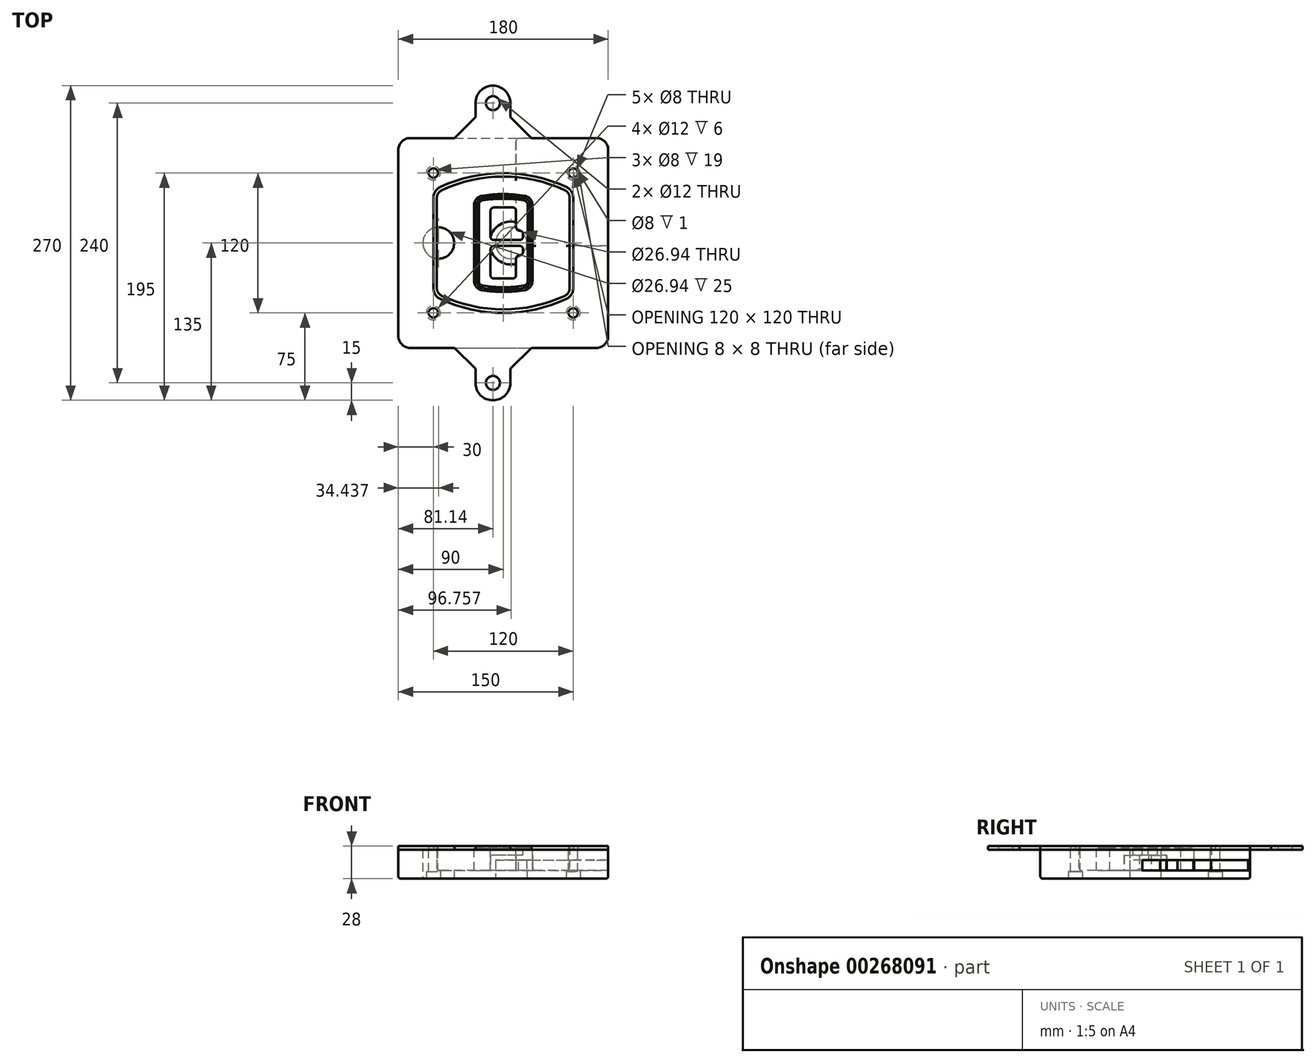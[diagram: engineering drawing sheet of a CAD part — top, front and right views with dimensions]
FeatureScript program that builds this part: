
annotation { "Feature Type Name" : "Feature", "Feature Type Description" : "" }
export const myFeature = defineFeature(function(context is Context, id is Id, definition is map)
    precondition{}
    {
        {
            var Q0;
            Q0=qCreatedBy(makeId("Top.planeOp"),FACE);
            var sketch = newSketch(context, id + "F0", { "sketchPlane" : qUnion([Q0])});
            skPoint(sketch, "E0.rect.middle", {"position": v(0, 0) * mm});
            skLineSegment(sketch, "E1.bottom", {"start": v(-80, -90) * mm, "end": v(80, -90) * mm});
            skLineSegment(sketch, "E1.top", {"start": v(-80, 90) * mm, "end": v(80, 90) * mm});
            skLineSegment(sketch, "E1.left", {"start": v(-90, -80) * mm, "end": v(-90, 80) * mm});
            skLineSegment(sketch, "E1.right", {"start": v(90, -80) * mm, "end": v(90, 80) * mm});
            skLineSegment(sketch, "E2", {"start": v(-90, 90) * mm, "end": v(90, -90) * mm, "construction": true});
            skLineSegment(sketch, "E3", {"start": v(90, 90) * mm, "end": v(-90, -90) * mm, "construction": true});
            skCircle(sketch, "E4", {"center": v(-60, 60) * mm, "radius": 4 * mm});
            skCircle(sketch, "E5", {"center": v(60, 60) * mm, "radius": 4 * mm});
            skCircle(sketch, "E6", {"center": v(60, -60) * mm, "radius": 4 * mm});
            skCircle(sketch, "E7", {"center": v(-60, -60) * mm, "radius": 4 * mm});
            skLineSegment(sketch, "E8", {"start": v(-60, 60) * mm, "end": v(60, 60) * mm, "construction": true});
            skLineSegment(sketch, "E9", {"start": v(60, 60) * mm, "end": v(60, -60) * mm, "construction": true});
            skLineSegment(sketch, "E10", {"start": v(60, -60) * mm, "end": v(-60, -60) * mm, "construction": true});
            skLineSegment(sketch, "E11", {"start": v(-60, -60) * mm, "end": v(-60, 60) * mm, "construction": true});
            skLineSegment(sketch, "E12", {"start": v(-60, 38.83) * mm, "end": v(-60, -38.83) * mm});
            skLineSegment(sketch, "E13", {"start": v(60, 38.83) * mm, "end": v(60, -38.83) * mm});
            skArc(sketch, "E14", {"start": v(54.26, 47.88) * mm, "mid": v(0, 60) * mm, "end": v(-54.26, 47.88) * mm});
            skArc(sketch, "E15", {"start": v(-54.26, -47.88) * mm, "mid": v(0, -60) * mm, "end": v(54.26, -47.88) * mm});
            skLineSegment(sketch, "E16", {"start": v(-60, 0) * mm, "end": v(60, 0) * mm, "construction": true});
            skPoint(sketch, "E17.visualSharp", {"position": v(-60, -45) * mm});
            skArc(sketch, "E17.filletArc", {"start": v(-60, -38.83) * mm, "mid": v(-58.44, -44.2) * mm, "end": v(-54.26, -47.88) * mm});
            skPoint(sketch, "E18.visualSharp", {"position": v(-60, 45) * mm});
            skArc(sketch, "E18.filletArc", {"start": v(-54.26, 47.88) * mm, "mid": v(-58.44, 44.2) * mm, "end": v(-60, 38.83) * mm});
            skPoint(sketch, "E19.visualSharp", {"position": v(60, 45) * mm});
            skArc(sketch, "E19.filletArc", {"start": v(60, 38.83) * mm, "mid": v(58.44, 44.2) * mm, "end": v(54.26, 47.88) * mm});
            skPoint(sketch, "E20.visualSharp", {"position": v(60, -45) * mm});
            skArc(sketch, "E20.filletArc", {"start": v(54.26, -47.88) * mm, "mid": v(58.44, -44.2) * mm, "end": v(60, -38.83) * mm});
            skPoint(sketch, "E21.visualSharp", {"position": v(-90, 90) * mm});
            skArc(sketch, "E21.filletArc", {"start": v(-80, 90) * mm, "mid": v(-87.07, 87.07) * mm, "end": v(-90, 80) * mm});
            skPoint(sketch, "E22.visualSharp", {"position": v(90, 90) * mm});
            skArc(sketch, "E22.filletArc", {"start": v(90, 80) * mm, "mid": v(87.07, 87.07) * mm, "end": v(80, 90) * mm});
            skPoint(sketch, "E23.visualSharp", {"position": v(90, -90) * mm});
            skArc(sketch, "E23.filletArc", {"start": v(80, -90) * mm, "mid": v(87.07, -87.07) * mm, "end": v(90, -80) * mm});
            skPoint(sketch, "E24.visualSharp", {"position": v(-90, -90) * mm});
            skArc(sketch, "E24.filletArc", {"start": v(-90, -80) * mm, "mid": v(-87.07, -87.07) * mm, "end": v(-80, -90) * mm});
            skArc(sketch, "E25.0", {"start": v(57, 38.83) * mm, "mid": v(55.9, 42.58) * mm, "end": v(52.98, 45.17) * mm});
            skLineSegment(sketch, "E25.1", {"start": v(57, 38.83) * mm, "end": v(57, -38.83) * mm});
            skArc(sketch, "E25.2", {"start": v(52.98, -45.17) * mm, "mid": v(55.9, -42.58) * mm, "end": v(57, -38.83) * mm});
            skArc(sketch, "E25.3", {"start": v(-52.98, -45.17) * mm, "mid": v(0, -57) * mm, "end": v(52.98, -45.17) * mm});
            skArc(sketch, "E25.4", {"start": v(-57, -38.83) * mm, "mid": v(-55.9, -42.58) * mm, "end": v(-52.98, -45.17) * mm});
            skArc(sketch, "E25.5", {"start": v(52.98, 45.17) * mm, "mid": v(0, 57) * mm, "end": v(-52.98, 45.17) * mm});
            skLineSegment(sketch, "E25.6", {"start": v(-57, 38.83) * mm, "end": v(-57, -38.83) * mm});
            skArc(sketch, "E25.7", {"start": v(-52.98, 45.17) * mm, "mid": v(-55.9, 42.58) * mm, "end": v(-57, 38.83) * mm});
            skArc(sketch, "E26.0", {"start": v(-55.96, 51.5) * mm, "mid": v(-61.82, 46.33) * mm, "end": v(-64, 38.83) * mm});
            skArc(sketch, "E26.1", {"start": v(55.96, 51.5) * mm, "mid": v(0, 64) * mm, "end": v(-55.96, 51.5) * mm});
            skArc(sketch, "E26.2", {"start": v(64, 38.83) * mm, "mid": v(61.82, 46.33) * mm, "end": v(55.96, 51.5) * mm});
            skLineSegment(sketch, "E26.3", {"start": v(64, 38.83) * mm, "end": v(64, -38.83) * mm});
            skArc(sketch, "E26.4", {"start": v(55.96, -51.5) * mm, "mid": v(61.82, -46.33) * mm, "end": v(64, -38.83) * mm});
            skLineSegment(sketch, "E26.5", {"start": v(-64, 38.83) * mm, "end": v(-64, -38.83) * mm});
            skArc(sketch, "E26.6", {"start": v(-55.96, -51.5) * mm, "mid": v(0, -64) * mm, "end": v(55.96, -51.5) * mm});
            skArc(sketch, "E26.7", {"start": v(-64, -38.83) * mm, "mid": v(-61.82, -46.33) * mm, "end": v(-55.96, -51.5) * mm});
            skSolve(sketch);
        }
        {
            var Q0;
            Q0=makeQuery(id+"F0.imprint","IMPRINT",FACE,{"disambiguationData":[TD([[makeQuery(id+"F0.imprint","IMPRINT",EDGE,{"derivedFrom":sQuery(id+"F0.wireOp",EDGE,"E1.bottom")}),1.0]])]});
            var Q1;
            Q1=makeQuery(id+"F0.imprint","IMPRINT",FACE,{"disambiguationData":[TD([[makeQuery(id+"F0.imprint","IMPRINT",EDGE,{"derivedFrom":sQuery(id+"F0.wireOp",EDGE,"E12")}),1.0]])]});
            var Q2;
            Q2=makeQuery(id+"F0.imprint","IMPRINT",FACE,{"disambiguationData":[TD([[makeQuery(id+"F0.imprint","IMPRINT",EDGE,{"derivedFrom":sQuery(id+"F0.wireOp",EDGE,"E25.0")}),1.0]])]});
            var Q3;
            Q3=makeQuery(id+"F0.imprint","IMPRINT",FACE,{"disambiguationData":[TD([[makeQuery(id+"F0.imprint","IMPRINT",EDGE,{"derivedFrom":sQuery(id+"F0.wireOp",EDGE,"E12")}),-1.0]])]});
            extrude(context, id + "F1", {"entities" : qUnion([Q0, Q1, Q2, Q3]), "oppositeDirection" : true, "depth" : 25 * mm});
        }
        {
            var Q0;
            Q0=makeQuery(id+"F0.imprint","IMPRINT",FACE,{"disambiguationData":[TD([[makeQuery(id+"F0.imprint","IMPRINT",EDGE,{"derivedFrom":sQuery(id+"F0.wireOp",EDGE,"E12")}),1.0]])]});
            extrude(context, id + "F2", {"entities" : qUnion([Q0]), "operationType" : NewBodyOperationType.ADD, "depth" : 3 * mm});
        }
        {
            var Q0;
            Q0=makeQuery(id+"F0.imprint","IMPRINT",FACE,{"disambiguationData":[TD([[makeQuery(id+"F0.imprint","IMPRINT",EDGE,{"derivedFrom":sQuery(id+"F0.wireOp",EDGE,"E25.0")}),1.0]])]});
            extrude(context, id + "F3", {"entities" : qUnion([Q0]), "operationType" : NewBodyOperationType.REMOVE, "oppositeDirection" : true, "depth" : 18 * mm});
        }
        {
            var Q0;
            Q0=makeQuery(id+"F2.opExtrude","CAP_FACE",FACE,{"disambiguationData":[OSD([sQuery(id+"F0.wireOp",EDGE,"E12"),sQuery(id+"F0.wireOp",EDGE,"E13"),sQuery(id+"F0.wireOp",EDGE,"E14"),sQuery(id+"F0.wireOp",EDGE,"E15"),sQuery(id+"F0.wireOp",EDGE,"E17.filletArc"),sQuery(id+"F0.wireOp",EDGE,"E18.filletArc"),sQuery(id+"F0.wireOp",EDGE,"E19.filletArc"),sQuery(id+"F0.wireOp",EDGE,"E20.filletArc"),sQuery(id+"F0.wireOp",EDGE,"E25.0"),sQuery(id+"F0.wireOp",EDGE,"E25.1"),sQuery(id+"F0.wireOp",EDGE,"E25.2"),sQuery(id+"F0.wireOp",EDGE,"E25.3"),sQuery(id+"F0.wireOp",EDGE,"E25.4"),sQuery(id+"F0.wireOp",EDGE,"E25.5"),sQuery(id+"F0.wireOp",EDGE,"E25.6"),sQuery(id+"F0.wireOp",EDGE,"E25.7")])],"isStart":false});
            var sketch = newSketch(context, id + "F4", { "sketchPlane" : qUnion([Q0])});
            skArc(sketch, "E27.0", {"start": v(-18.34, -40.45) * mm, "mid": v(0, -42) * mm, "end": v(18.34, -40.45) * mm});
            skArc(sketch, "E28.0", {"start": v(18.34, 40.45) * mm, "mid": v(0, 42) * mm, "end": v(-18.34, 40.45) * mm});
            skLineSegment(sketch, "E29", {"start": v(-25, 32.57) * mm, "end": v(-25, -32.57) * mm});
            skLineSegment(sketch, "E30", {"start": v(25, 32.57) * mm, "end": v(25, -32.57) * mm});
            skLineSegment(sketch, "E31", {"start": v(-25, 39.1) * mm, "end": v(25, 39.1) * mm, "construction": true});
            skLineSegment(sketch, "E32", {"start": v(-25, -39.1) * mm, "end": v(25, -39.1) * mm, "construction": true});
            skPoint(sketch, "E33.visualSharp", {"position": v(-25, 39.1) * mm});
            skArc(sketch, "E33.filletArc", {"start": v(-18.34, 40.45) * mm, "mid": v(-23.11, 37.73) * mm, "end": v(-25, 32.57) * mm});
            skPoint(sketch, "E34.visualSharp", {"position": v(25, 39.1) * mm});
            skArc(sketch, "E34.filletArc", {"start": v(25, 32.57) * mm, "mid": v(23.11, 37.73) * mm, "end": v(18.34, 40.45) * mm});
            skPoint(sketch, "E35.visualSharp", {"position": v(25, -39.1) * mm});
            skArc(sketch, "E35.filletArc", {"start": v(18.34, -40.45) * mm, "mid": v(23.11, -37.73) * mm, "end": v(25, -32.57) * mm});
            skPoint(sketch, "E36.visualSharp", {"position": v(-25, -39.1) * mm});
            skArc(sketch, "E36.filletArc", {"start": v(-25, -32.57) * mm, "mid": v(-23.11, -37.73) * mm, "end": v(-18.34, -40.45) * mm});
            skArc(sketch, "E37.0", {"start": v(52.98, 45.17) * mm, "mid": v(0, 57) * mm, "end": v(-52.98, 45.17) * mm});
            skArc(sketch, "E37.1", {"start": v(-52.98, 45.17) * mm, "mid": v(-55.9, 42.58) * mm, "end": v(-57, 38.83) * mm});
            skLineSegment(sketch, "E37.2", {"start": v(-57, 38.83) * mm, "end": v(-57, -38.83) * mm});
            skArc(sketch, "E37.3", {"start": v(-57, -38.83) * mm, "mid": v(-55.9, -42.58) * mm, "end": v(-52.98, -45.17) * mm});
            skArc(sketch, "E37.4", {"start": v(-52.98, -45.17) * mm, "mid": v(0, -57) * mm, "end": v(52.98, -45.17) * mm});
            skArc(sketch, "E37.5", {"start": v(52.98, -45.17) * mm, "mid": v(55.9, -42.58) * mm, "end": v(57, -38.83) * mm});
            skLineSegment(sketch, "E37.6", {"start": v(57, 38.83) * mm, "end": v(57, -38.83) * mm});
            skArc(sketch, "E37.7", {"start": v(57, 38.83) * mm, "mid": v(55.9, 42.58) * mm, "end": v(52.98, 45.17) * mm});
            skLineSegment(sketch, "E38.0", {"start": v(23, 32.57) * mm, "end": v(23, -32.57) * mm});
            skArc(sketch, "E38.1", {"start": v(18, -38.48) * mm, "mid": v(21.58, -36.44) * mm, "end": v(23, -32.57) * mm});
            skArc(sketch, "E38.2", {"start": v(-18, -38.48) * mm, "mid": v(0, -40) * mm, "end": v(18, -38.48) * mm});
            skArc(sketch, "E38.3", {"start": v(-23, -32.57) * mm, "mid": v(-21.58, -36.44) * mm, "end": v(-18, -38.48) * mm});
            skLineSegment(sketch, "E38.4", {"start": v(-23, 32.57) * mm, "end": v(-23, -32.57) * mm});
            skArc(sketch, "E38.5", {"start": v(23, 32.57) * mm, "mid": v(21.58, 36.44) * mm, "end": v(18, 38.48) * mm});
            skArc(sketch, "E38.6", {"start": v(-18, 38.48) * mm, "mid": v(-21.58, 36.44) * mm, "end": v(-23, 32.57) * mm});
            skArc(sketch, "E38.7", {"start": v(18, 38.48) * mm, "mid": v(0, 40) * mm, "end": v(-18, 38.48) * mm});
            skArc(sketch, "E39.0", {"start": v(21, 32.57) * mm, "mid": v(20.06, 35.15) * mm, "end": v(17.67, 36.5) * mm});
            skLineSegment(sketch, "E39.1", {"start": v(21, 32.57) * mm, "end": v(21, -32.57) * mm});
            skArc(sketch, "E39.2", {"start": v(17.67, -36.5) * mm, "mid": v(20.06, -35.15) * mm, "end": v(21, -32.57) * mm});
            skArc(sketch, "E39.3", {"start": v(-17.67, -36.5) * mm, "mid": v(0, -38) * mm, "end": v(17.67, -36.5) * mm});
            skArc(sketch, "E39.4", {"start": v(-21, -32.57) * mm, "mid": v(-20.06, -35.15) * mm, "end": v(-17.67, -36.5) * mm});
            skArc(sketch, "E39.5", {"start": v(17.67, 36.5) * mm, "mid": v(0, 38) * mm, "end": v(-17.67, 36.5) * mm});
            skLineSegment(sketch, "E39.6", {"start": v(-21, 32.57) * mm, "end": v(-21, -32.57) * mm});
            skArc(sketch, "E39.7", {"start": v(-17.67, 36.5) * mm, "mid": v(-20.06, 35.15) * mm, "end": v(-21, 32.57) * mm});
            skLineSegment(sketch, "E40", {"start": v(-25, 0) * mm, "end": v(25, 0) * mm, "construction": true});
            skLineSegment(sketch, "E41", {"start": v(-11, 5.5) * mm, "end": v(-11, 27.5) * mm});
            skLineSegment(sketch, "E42", {"start": v(-8, 30.5) * mm, "end": v(8, 30.5) * mm});
            skLineSegment(sketch, "E43", {"start": v(11, 27.5) * mm, "end": v(11, 13.5) * mm});
            skLineSegment(sketch, "E44", {"start": v(14, 10.5) * mm, "end": v(14, 10.5) * mm});
            skLineSegment(sketch, "E45", {"start": v(17, 7.5) * mm, "end": v(17, 5.5) * mm});
            skLineSegment(sketch, "E46", {"start": v(14, 2.5) * mm, "end": v(-8, 2.5) * mm});
            skPoint(sketch, "E47.visualSharp", {"position": v(-11, 30.5) * mm});
            skArc(sketch, "E47.filletArc", {"start": v(-8, 30.5) * mm, "mid": v(-10.12, 29.62) * mm, "end": v(-11, 27.5) * mm});
            skPoint(sketch, "E48.visualSharp", {"position": v(11, 30.5) * mm});
            skArc(sketch, "E48.filletArc", {"start": v(11, 27.5) * mm, "mid": v(10.12, 29.62) * mm, "end": v(8, 30.5) * mm});
            skPoint(sketch, "E49.visualSharp", {"position": v(11, 10.5) * mm});
            skArc(sketch, "E49.filletArc", {"start": v(11, 13.5) * mm, "mid": v(11.88, 11.38) * mm, "end": v(14, 10.5) * mm});
            skPoint(sketch, "E50.visualSharp", {"position": v(17, 10.5) * mm});
            skArc(sketch, "E50.filletArc", {"start": v(17, 7.5) * mm, "mid": v(16.12, 9.62) * mm, "end": v(14, 10.5) * mm});
            skPoint(sketch, "E51.visualSharp", {"position": v(17, 2.5) * mm});
            skArc(sketch, "E51.filletArc", {"start": v(14, 2.5) * mm, "mid": v(16.12, 3.38) * mm, "end": v(17, 5.5) * mm});
            skPoint(sketch, "E52.visualSharp", {"position": v(-11, 2.5) * mm});
            skArc(sketch, "E52.filletArc", {"start": v(-11, 5.5) * mm, "mid": v(-10.12, 3.38) * mm, "end": v(-8, 2.5) * mm});
            skLineSegment(sketch, "E53.0.MirrorCS", {"start": v(14, -2.5) * mm, "end": v(-8, -2.5) * mm});
            skArc(sketch, "E54.0.MirrorCS", {"start": v(-11, -5.5) * mm, "mid": v(-10.12, -3.38) * mm, "end": v(-8, -2.5) * mm});
            skLineSegment(sketch, "E55.0.MirrorCS", {"start": v(-11, -5.5) * mm, "end": v(-11, -27.5) * mm});
            skArc(sketch, "E56.0.MirrorCS", {"start": v(-8, -30.5) * mm, "mid": v(-10.12, -29.62) * mm, "end": v(-11, -27.5) * mm});
            skLineSegment(sketch, "E57.0.MirrorCS", {"start": v(-8, -30.5) * mm, "end": v(8, -30.5) * mm});
            skArc(sketch, "E58.0.MirrorCS", {"start": v(11, -27.5) * mm, "mid": v(10.12, -29.62) * mm, "end": v(8, -30.5) * mm});
            skLineSegment(sketch, "E59.0.MirrorCS", {"start": v(11, -27.5) * mm, "end": v(11, -13.5) * mm});
            skArc(sketch, "E60.0.MirrorCS", {"start": v(11, -13.5) * mm, "mid": v(11.88, -11.38) * mm, "end": v(14, -10.5) * mm});
            skArc(sketch, "E61.0.MirrorCS", {"start": v(17, -7.5) * mm, "mid": v(16.12, -9.62) * mm, "end": v(14, -10.5) * mm});
            skLineSegment(sketch, "E62.0.MirrorCS", {"start": v(17, -7.5) * mm, "end": v(17, -5.5) * mm});
            skArc(sketch, "E63.0.MirrorCS", {"start": v(14, -2.5) * mm, "mid": v(16.12, -3.38) * mm, "end": v(17, -5.5) * mm});
            skSolve(sketch);
        }
        {
            var Q0;
            Q0=makeQuery(id+"F4.imprint","IMPRINT",FACE,{"disambiguationData":[TD([[makeQuery(id+"F4.imprint","IMPRINT",EDGE,{"derivedFrom":sQuery(id+"F4.wireOp",EDGE,"E27.0")}),1.0]])]});
            var Q1;
            Q1=makeQuery(id+"F4.imprint","IMPRINT",FACE,{"disambiguationData":[TD([[makeQuery(id+"F4.imprint","IMPRINT",EDGE,{"derivedFrom":sQuery(id+"F4.wireOp",EDGE,"E38.0")}),-1.0]])]});
            var Q2;
            Q2=makeQuery(id+"F4.imprint","IMPRINT",FACE,{"disambiguationData":[TD([[makeQuery(id+"F4.imprint","IMPRINT",EDGE,{"derivedFrom":sQuery(id+"F4.wireOp",EDGE,"E39.0")}),1.0]])]});
            extrude(context, id + "F5", {"entities" : qUnion([Q0, Q1, Q2]), "operationType" : NewBodyOperationType.ADD, "endBound" : BoundingType.UP_TO_NEXT, "oppositeDirection" : true, "depth" : 25 * mm});
        }
        {
            var Q0;
            Q0=makeQuery(id+"F4.imprint","IMPRINT",FACE,{"disambiguationData":[TD([[makeQuery(id+"F4.imprint","IMPRINT",EDGE,{"derivedFrom":sQuery(id+"F4.wireOp",EDGE,"E38.0")}),-1.0]])]});
            extrude(context, id + "F6", {"entities" : qUnion([Q0]), "operationType" : NewBodyOperationType.REMOVE, "oppositeDirection" : true, "depth" : 2 * mm});
        }
        {
            var Q0;
            Q0=makeQuery(id+"F1.opExtrude","CAP_FACE",FACE,{"disambiguationData":[OSD([sQuery(id+"F0.wireOp",EDGE,"E1.bottom"),sQuery(id+"F0.wireOp",EDGE,"E1.top"),sQuery(id+"F0.wireOp",EDGE,"E1.left"),sQuery(id+"F0.wireOp",EDGE,"E1.right"),sQuery(id+"F0.wireOp",EDGE,"E4"),sQuery(id+"F0.wireOp",EDGE,"E5"),sQuery(id+"F0.wireOp",EDGE,"E6"),sQuery(id+"F0.wireOp",EDGE,"E7"),sQuery(id+"F0.wireOp",EDGE,"E21.filletArc"),sQuery(id+"F0.wireOp",EDGE,"E22.filletArc"),sQuery(id+"F0.wireOp",EDGE,"E23.filletArc"),sQuery(id+"F0.wireOp",EDGE,"E24.filletArc")])],"isStart":false});
            var sketch = newSketch(context, id + "F7", { "sketchPlane" : qUnion([Q0])});
            skCircle(sketch, "E64", {"center": v(6.76, 0) * mm, "radius": 13.47 * mm});
            skCircle(sketch, "E65", {"center": v(-55.56, 0) * mm, "radius": 13.47 * mm});
            skLineSegment(sketch, "E66", {"start": v(90, 0) * mm, "end": v(-90, 0) * mm});
            skCircle(sketch, "E67", {"center": v(6.76, 0) * mm, "radius": 18.47 * mm});
            skCircle(sketch, "E68", {"center": v(60, -60) * mm, "radius": 6 * mm});
            skCircle(sketch, "E69", {"center": v(-60, -60) * mm, "radius": 6 * mm});
            skCircle(sketch, "E70", {"center": v(-60, 60) * mm, "radius": 6 * mm});
            skCircle(sketch, "E71", {"center": v(60, 60) * mm, "radius": 6 * mm});
            skSolve(sketch);
        }
        {
            var Q0;
            {var subQ1=sQuery(id+"F7.wireOp",EDGE,"E66");var subQ4=sQuery(id+"F7.wireOp",EDGE,"E64");var subQ6=makeQuery(id+"F7.imprint","INTERSECT",VERTEX,{"disambiguationData":[OD(0.0)],"derivedFrom":[subQ4,subQ1]});Q0=makeQuery(id+"F7.imprint","IMPRINT",FACE,{"disambiguationData":[TD([[makeQuery(id+"F7.imprint","IMPRINT",EDGE,{"disambiguationData":[TD([[subQ6,-1.0]])],"derivedFrom":subQ4}),-1.0]])]});}
            var Q1;
            {var subQ0=sQuery(id+"F7.wireOp",EDGE,"E66");var subQ1=sQuery(id+"F7.wireOp",EDGE,"E64");var subQ3=makeQuery(id+"F7.imprint","INTERSECT",VERTEX,{"disambiguationData":[OD(0.0)],"derivedFrom":[subQ1,subQ0]});Q1=makeQuery(id+"F7.imprint","IMPRINT",FACE,{"disambiguationData":[TD([[makeQuery(id+"F7.imprint","IMPRINT",EDGE,{"disambiguationData":[TD([[subQ3,-1.0]])],"derivedFrom":subQ1}),1.0]])]});}
            var Q2;
            {var subQ0=sQuery(id+"F7.wireOp",EDGE,"E66");var subQ1=sQuery(id+"F7.wireOp",EDGE,"E64");var subQ3=makeQuery(id+"F7.imprint","INTERSECT",VERTEX,{"disambiguationData":[OD(0.0)],"derivedFrom":[subQ1,subQ0]});Q2=makeQuery(id+"F7.imprint","IMPRINT",FACE,{"disambiguationData":[TD([[makeQuery(id+"F7.imprint","IMPRINT",EDGE,{"disambiguationData":[TD([[subQ3,1.0]])],"derivedFrom":subQ1}),1.0]])]});}
            var Q3;
            {var subQ1=sQuery(id+"F7.wireOp",EDGE,"E66");var subQ4=sQuery(id+"F7.wireOp",EDGE,"E64");var subQ6=makeQuery(id+"F7.imprint","INTERSECT",VERTEX,{"disambiguationData":[OD(0.0)],"derivedFrom":[subQ4,subQ1]});Q3=makeQuery(id+"F7.imprint","IMPRINT",FACE,{"disambiguationData":[TD([[makeQuery(id+"F7.imprint","IMPRINT",EDGE,{"disambiguationData":[TD([[subQ6,1.0]])],"derivedFrom":subQ4}),-1.0]])]});}
            extrude(context, id + "F8", {"entities" : qUnion([Q0, Q1, Q2, Q3]), "operationType" : NewBodyOperationType.ADD, "oppositeDirection" : true, "depth" : 20 * mm});
        }
        {
            var Q0;
            {var subQ0=sQuery(id+"F7.wireOp",EDGE,"E66");var subQ1=sQuery(id+"F7.wireOp",EDGE,"E64");var subQ3=makeQuery(id+"F7.imprint","INTERSECT",VERTEX,{"disambiguationData":[OD(0.0)],"derivedFrom":[subQ1,subQ0]});Q0=makeQuery(id+"F7.imprint","IMPRINT",FACE,{"disambiguationData":[TD([[makeQuery(id+"F7.imprint","IMPRINT",EDGE,{"disambiguationData":[TD([[subQ3,-1.0]])],"derivedFrom":subQ1}),1.0]])]});}
            var Q1;
            {var subQ0=sQuery(id+"F7.wireOp",EDGE,"E66");var subQ1=sQuery(id+"F7.wireOp",EDGE,"E64");var subQ3=makeQuery(id+"F7.imprint","INTERSECT",VERTEX,{"disambiguationData":[OD(0.0)],"derivedFrom":[subQ1,subQ0]});Q1=makeQuery(id+"F7.imprint","IMPRINT",FACE,{"disambiguationData":[TD([[makeQuery(id+"F7.imprint","IMPRINT",EDGE,{"disambiguationData":[TD([[subQ3,1.0]])],"derivedFrom":subQ1}),1.0]])]});}
            extrude(context, id + "F9", {"entities" : qUnion([Q0, Q1]), "operationType" : NewBodyOperationType.REMOVE, "oppositeDirection" : true, "depth" : 16 * mm});
        }
        {
            var Q0;
            {var subQ0=sQuery(id+"F7.wireOp",EDGE,"E66");var subQ1=sQuery(id+"F7.wireOp",EDGE,"E65");var subQ3=makeQuery(id+"F7.imprint","INTERSECT",VERTEX,{"disambiguationData":[OD(0.0)],"derivedFrom":[subQ1,subQ0]});Q0=makeQuery(id+"F7.imprint","IMPRINT",FACE,{"disambiguationData":[TD([[makeQuery(id+"F7.imprint","IMPRINT",EDGE,{"disambiguationData":[TD([[subQ3,-1.0]])],"derivedFrom":subQ1}),1.0]])]});}
            var Q1;
            {var subQ0=sQuery(id+"F7.wireOp",EDGE,"E66");var subQ1=sQuery(id+"F7.wireOp",EDGE,"E65");var subQ3=makeQuery(id+"F7.imprint","INTERSECT",VERTEX,{"disambiguationData":[OD(0.0)],"derivedFrom":[subQ1,subQ0]});Q1=makeQuery(id+"F7.imprint","IMPRINT",FACE,{"disambiguationData":[TD([[makeQuery(id+"F7.imprint","IMPRINT",EDGE,{"disambiguationData":[TD([[subQ3,1.0]])],"derivedFrom":subQ1}),1.0]])]});}
            extrude(context, id + "F10", {"entities" : qUnion([Q0, Q1]), "operationType" : NewBodyOperationType.REMOVE, "oppositeDirection" : true, "depth" : 25 * mm});
        }
        {
            var Q0;
            Q0=makeQuery(id+"F7.imprint","IMPRINT",FACE,{"disambiguationData":[TD([[makeQuery(id+"F7.imprint","IMPRINT",EDGE,{"derivedFrom":sQuery(id+"F7.wireOp",EDGE,"E68")}),1.0]])]});
            var Q1;
            Q1=makeQuery(id+"F7.imprint","IMPRINT",FACE,{"disambiguationData":[TD([[makeQuery(id+"F7.imprint","IMPRINT",EDGE,{"derivedFrom":makeQuery(id+"F1.opExtrude","CAP_EDGE",EDGE,{"disambiguationData":[OSD([sQuery(id+"F0.wireOp",EDGE,"E5")])],"isStart":false})}),-1.0]])]});
            var Q2;
            Q2=makeQuery(id+"F7.imprint","IMPRINT",FACE,{"disambiguationData":[TD([[makeQuery(id+"F7.imprint","IMPRINT",EDGE,{"derivedFrom":sQuery(id+"F7.wireOp",EDGE,"E69")}),1.0]])]});
            var Q3;
            Q3=makeQuery(id+"F7.imprint","IMPRINT",FACE,{"disambiguationData":[TD([[makeQuery(id+"F7.imprint","IMPRINT",EDGE,{"derivedFrom":makeQuery(id+"F1.opExtrude","CAP_EDGE",EDGE,{"disambiguationData":[OSD([sQuery(id+"F0.wireOp",EDGE,"E4")])],"isStart":false})}),-1.0]])]});
            var Q4;
            Q4=makeQuery(id+"F7.imprint","IMPRINT",FACE,{"disambiguationData":[TD([[makeQuery(id+"F7.imprint","IMPRINT",EDGE,{"derivedFrom":sQuery(id+"F7.wireOp",EDGE,"E70")}),1.0]])]});
            var Q5;
            Q5=makeQuery(id+"F7.imprint","IMPRINT",FACE,{"disambiguationData":[TD([[makeQuery(id+"F7.imprint","IMPRINT",EDGE,{"derivedFrom":makeQuery(id+"F1.opExtrude","CAP_EDGE",EDGE,{"disambiguationData":[OSD([sQuery(id+"F0.wireOp",EDGE,"E7")])],"isStart":false})}),-1.0]])]});
            var Q6;
            Q6=makeQuery(id+"F7.imprint","IMPRINT",FACE,{"disambiguationData":[TD([[makeQuery(id+"F7.imprint","IMPRINT",EDGE,{"derivedFrom":sQuery(id+"F7.wireOp",EDGE,"E71")}),1.0]])]});
            var Q7;
            Q7=makeQuery(id+"F7.imprint","IMPRINT",FACE,{"disambiguationData":[TD([[makeQuery(id+"F7.imprint","IMPRINT",EDGE,{"derivedFrom":makeQuery(id+"F1.opExtrude","CAP_EDGE",EDGE,{"disambiguationData":[OSD([sQuery(id+"F0.wireOp",EDGE,"E6")])],"isStart":false})}),-1.0]])]});
            extrude(context, id + "F11", {"entities" : qUnion([Q0, Q1, Q2, Q3, Q4, Q5, Q6, Q7]), "operationType" : NewBodyOperationType.REMOVE, "oppositeDirection" : true, "depth" : 6 * mm});
        }
        {
            var Q0;
            Q0=makeQuery(id+"F9.boolean.opBoolean","COPY",FACE,{"derivedFrom":makeQuery(id+"F9.opExtrude","CAP_FACE",FACE,{"disambiguationData":[OSD([sQuery(id+"F7.wireOp",EDGE,"E64")])],"isStart":false})});
            var sketch = newSketch(context, id + "F12", { "sketchPlane" : qUnion([Q0])});
            skArc(sketch, "E72.0", {"start": v(11, -88.19) * mm, "mid": v(97.1, -83.6) * mm, "end": v(92.5, 2.5) * mm});
            skLineSegment(sketch, "E72.1", {"start": v(11, -17.97) * mm, "end": v(11, -17.97) * mm});
            skLineSegment(sketch, "E73", {"start": v(92.5, -105.13) * mm, "end": v(102.3, -105.13) * mm});
            skLineSegment(sketch, "E74.0", {"start": v(92.5, 2.5) * mm, "end": v(14, 2.5) * mm});
            skArc(sketch, "E74.1", {"start": v(14, 2.5) * mm, "mid": v(16.12, 3.38) * mm, "end": v(17, 5.5) * mm});
            skLineSegment(sketch, "E74.2", {"start": v(17, 7.5) * mm, "end": v(17, 5.5) * mm});
            skArc(sketch, "E74.3", {"start": v(17, 7.5) * mm, "mid": v(16.12, 9.62) * mm, "end": v(14, 10.5) * mm});
            skArc(sketch, "E74.4", {"start": v(11, 13.5) * mm, "mid": v(11.88, 11.38) * mm, "end": v(14, 10.5) * mm});
            skLineSegment(sketch, "E74.5", {"start": v(11, 13.5) * mm, "end": v(11, -88.19) * mm});
            skLineSegment(sketch, "E74.7", {"start": v(92.5, -2.5) * mm, "end": v(14, -2.5) * mm});
            skArc(sketch, "E74.8", {"start": v(14, -2.5) * mm, "mid": v(16.12, -3.38) * mm, "end": v(17, -5.5) * mm});
            skLineSegment(sketch, "E74.9", {"start": v(17, -7.5) * mm, "end": v(17, -5.5) * mm});
            skArc(sketch, "E74.10", {"start": v(17, -7.5) * mm, "mid": v(16.12, -9.62) * mm, "end": v(14, -10.5) * mm});
            skArc(sketch, "E74.11", {"start": v(11, -13.5) * mm, "mid": v(11.88, -11.38) * mm, "end": v(14, -10.5) * mm});
            skLineSegment(sketch, "E74.12", {"start": v(11, -17.97) * mm, "end": v(11, -13.5) * mm});
            skPoint(sketch, "E75.orphan", {"position": v(11, -27.5) * mm});
            skPoint(sketch, "E76.orphan", {"position": v(-8, -2.5) * mm});
            skPoint(sketch, "E77.orphan", {"position": v(-8, 2.5) * mm});
            skPoint(sketch, "E78.orphan", {"position": v(11, 27.5) * mm});
            skSolve(sketch);
        }
        {
            var Q0;
            {var subQ7=sQuery(id+"F12.wireOp",EDGE,"E72.0");var subQ14=sQuery(id+"F12.wireOp",EDGE,"E72.1");var subQ16=sQuery(id+"F12.wireOp",EDGE,"E74.1");var subQ18=sQuery(id+"F12.wireOp",EDGE,"E74.8");Q0=qUnion([makeQuery(id+"F12.imprint","IMPRINT",FACE,{"disambiguationData":[TD([[makeQuery(id+"F12.imprint","IMPRINT",EDGE,{"derivedFrom":subQ7}),1.0]])]}),makeQuery(id+"F12.imprint","IMPRINT",FACE,{"disambiguationData":[TD([[makeQuery(id+"F12.imprint","IMPRINT",EDGE,{"derivedFrom":subQ14}),1.0]])]}),makeQuery(id+"F12.imprint","IMPRINT",FACE,{"disambiguationData":[TD([[makeQuery(id+"F12.imprint","IMPRINT",EDGE,{"derivedFrom":subQ16}),1.0]])]}),makeQuery(id+"F12.imprint","IMPRINT",FACE,{"disambiguationData":[TD([[makeQuery(id+"F12.imprint","IMPRINT",EDGE,{"derivedFrom":subQ18}),-1.0]])]})]);}
            var Q1;
            Q1=makeQuery(id+"F5.boolean.opBoolean","SPLIT",FACE,{"disambiguationData":[TD([makeQuery(id+"F5.opExtrude","SWEPT_FACE",FACE,{"disambiguationData":[OSD([sQuery(id+"F4.wireOp",EDGE,"E41")])]})])],"derivedFrom":makeQuery(id+"F3.boolean.opBoolean","COPY",FACE,{"derivedFrom":makeQuery(id+"F3.opExtrude","CAP_FACE",FACE,{"disambiguationData":[OSD([sQuery(id+"F0.wireOp",EDGE,"E25.0"),sQuery(id+"F0.wireOp",EDGE,"E25.1"),sQuery(id+"F0.wireOp",EDGE,"E25.2"),sQuery(id+"F0.wireOp",EDGE,"E25.3"),sQuery(id+"F0.wireOp",EDGE,"E25.4"),sQuery(id+"F0.wireOp",EDGE,"E25.5"),sQuery(id+"F0.wireOp",EDGE,"E25.6"),sQuery(id+"F0.wireOp",EDGE,"E25.7")])],"isStart":false})})});
            extrude(context, id + "F13", {"entities" : qUnion([Q0]), "operationType" : NewBodyOperationType.REMOVE, "endBound" : BoundingType.UP_TO_SURFACE, "endBoundEntityFace" : qUnion([Q1]), "depth" : 25 * mm});
        }
        {
            var Q0;
            Q0=makeQuery(id+"F3.boolean.opBoolean","COPY",EDGE,{"derivedFrom":makeQuery(id+"F3.opExtrude","CAP_EDGE",EDGE,{"disambiguationData":[OSD([sQuery(id+"F0.wireOp",EDGE,"E25.6")])],"isStart":false})});
            var Q1;
            Q1=makeQuery(id+"F8.boolean.opBoolean","INTERSECT",EDGE,{"derivedFrom":[makeQuery(id+"F5.opExtrude","SWEPT_FACE",FACE,{"disambiguationData":[OSD([sQuery(id+"F4.wireOp",EDGE,"E30")])]}),makeQuery(id+"F8.opExtrude","CAP_FACE",FACE,{"disambiguationData":[OSD([sQuery(id+"F7.wireOp",EDGE,"E67")])],"isStart":false})]});
            var Q2;
            Q2=makeQuery(id+"F8.boolean.opBoolean","INTERSECT",EDGE,{"disambiguationData":[OD(1.0)],"derivedFrom":[makeQuery(id+"F5.opExtrude","SWEPT_FACE",FACE,{"disambiguationData":[OSD([sQuery(id+"F4.wireOp",EDGE,"E30")])]}),makeQuery(id+"F8.opExtrude","SWEPT_FACE",FACE,{"disambiguationData":[OSD([sQuery(id+"F7.wireOp",EDGE,"E67")])]})]});
            var Q3;
            {var subQ0=makeQuery(id+"F3.boolean.opBoolean","COPY",FACE,{"derivedFrom":makeQuery(id+"F3.opExtrude","CAP_FACE",FACE,{"disambiguationData":[OSD([sQuery(id+"F0.wireOp",EDGE,"E25.0"),sQuery(id+"F0.wireOp",EDGE,"E25.1"),sQuery(id+"F0.wireOp",EDGE,"E25.2"),sQuery(id+"F0.wireOp",EDGE,"E25.3"),sQuery(id+"F0.wireOp",EDGE,"E25.4"),sQuery(id+"F0.wireOp",EDGE,"E25.5"),sQuery(id+"F0.wireOp",EDGE,"E25.6"),sQuery(id+"F0.wireOp",EDGE,"E25.7")])],"isStart":false})});var subQ1=sQuery(id+"F4.wireOp",EDGE,"E30");Q3=makeQuery(id+"F8.boolean.opBoolean","SPLIT",EDGE,{"disambiguationData":[TD([makeQuery(id+"F5.opExtrude","SWEPT_FACE",FACE,{"disambiguationData":[OSD([sQuery(id+"F4.wireOp",EDGE,"E35.filletArc")])]})])],"derivedFrom":makeQuery(id+"F5.opExtrude","TWEAK_EDGE",EDGE,{"derivedFrom":[subQ0,makeQuery(id+"F4.imprint","IMPRINT",EDGE,{"derivedFrom":subQ1})]})});}
            var Q4;
            {var subQ0=sQuery(id+"F0.wireOp",EDGE,"E25.0");var subQ1=sQuery(id+"F0.wireOp",EDGE,"E25.1");var subQ2=sQuery(id+"F0.wireOp",EDGE,"E25.2");var subQ3=sQuery(id+"F0.wireOp",EDGE,"E25.3");var subQ4=sQuery(id+"F0.wireOp",EDGE,"E25.4");var subQ5=sQuery(id+"F0.wireOp",EDGE,"E25.5");var subQ6=sQuery(id+"F0.wireOp",EDGE,"E25.6");var subQ7=sQuery(id+"F0.wireOp",EDGE,"E25.7");Q4=makeQuery(id+"F8.boolean.opBoolean","INTERSECT",EDGE,{"derivedFrom":[makeQuery(id+"F5.boolean.opBoolean","SPLIT",FACE,{"disambiguationData":[TD([makeQuery(id+"F2.opExtrude","SWEPT_FACE",FACE,{"disambiguationData":[OSD([subQ0])]})])],"derivedFrom":makeQuery(id+"F3.boolean.opBoolean","COPY",FACE,{"derivedFrom":makeQuery(id+"F3.opExtrude","CAP_FACE",FACE,{"disambiguationData":[OSD([subQ0,subQ1,subQ2,subQ3,subQ4,subQ5,subQ6,subQ7])],"isStart":false})})}),makeQuery(id+"F8.opExtrude","SWEPT_FACE",FACE,{"disambiguationData":[OSD([sQuery(id+"F7.wireOp",EDGE,"E67")])]})]});}
            var Q5;
            Q5=makeQuery(id+"F8.boolean.opBoolean","INTERSECT",EDGE,{"disambiguationData":[OD(0.0)],"derivedFrom":[makeQuery(id+"F5.opExtrude","SWEPT_FACE",FACE,{"disambiguationData":[OSD([sQuery(id+"F4.wireOp",EDGE,"E30")])]}),makeQuery(id+"F8.opExtrude","SWEPT_FACE",FACE,{"disambiguationData":[OSD([sQuery(id+"F7.wireOp",EDGE,"E67")])]})]});
            fillet(context, id + "F14", {"entities" : qUnion([Q0, Q1, Q2, Q3, Q4, Q5]), "radius" : 3 * mm, "tangentPropagation" : true, "allowEdgeOverflow" : false});
        }
        {
            var Q0;
            Q0=makeQuery(id+"F1.opExtrude","CAP_EDGE",EDGE,{"disambiguationData":[OSD([sQuery(id+"F0.wireOp",EDGE,"E1.bottom")])],"isStart":false});
            fillet(context, id + "F15", {"entities" : qUnion([Q0]), "radius" : 2 * mm, "tangentPropagation" : true, "allowEdgeOverflow" : false});
        }
        {
            var Q0;
            Q0=qCreatedBy(makeId("Top.planeOp"),FACE);
            var sketch = newSketch(context, id + "F16", { "sketchPlane" : qUnion([Q0])});
            skLineSegment(sketch, "E79.0", {"start": v(-90, -80) * mm, "end": v(-90, 80) * mm});
            skArc(sketch, "E80.0", {"start": v(-80, 90) * mm, "mid": v(-87.07, 87.07) * mm, "end": v(-90, 80) * mm});
            skLineSegment(sketch, "E81.0", {"start": v(-80, 90) * mm, "end": v(80, 90) * mm});
            skArc(sketch, "E82.0", {"start": v(90, 80) * mm, "mid": v(87.07, 87.07) * mm, "end": v(80, 90) * mm});
            skLineSegment(sketch, "E83.0", {"start": v(90, -80) * mm, "end": v(90, 80) * mm});
            skArc(sketch, "E84.0", {"start": v(80, -90) * mm, "mid": v(87.07, -87.07) * mm, "end": v(90, -80) * mm});
            skLineSegment(sketch, "E85.0", {"start": v(-80, -90) * mm, "end": v(80, -90) * mm});
            skArc(sketch, "E86.0", {"start": v(-90, -80) * mm, "mid": v(-87.07, -87.07) * mm, "end": v(-80, -90) * mm});
            skCircle(sketch, "E87.0", {"center": v(-60, 60) * mm, "radius": 4 * mm});
            skCircle(sketch, "E88.0", {"center": v(60, 60) * mm, "radius": 4 * mm});
            skCircle(sketch, "E89.0", {"center": v(60, -60) * mm, "radius": 4 * mm});
            skCircle(sketch, "E90.0", {"center": v(-60, -60) * mm, "radius": 4 * mm});
            skArc(sketch, "E91.0", {"start": v(54.26, 47.88) * mm, "mid": v(0, 60) * mm, "end": v(-54.26, 47.88) * mm});
            skArc(sketch, "E92.0", {"start": v(-54.26, 47.88) * mm, "mid": v(-58.44, 44.2) * mm, "end": v(-60, 38.83) * mm});
            skLineSegment(sketch, "E93.0", {"start": v(-60, 38.83) * mm, "end": v(-60, -38.83) * mm});
            skArc(sketch, "E94.0", {"start": v(60, 38.83) * mm, "mid": v(58.44, 44.2) * mm, "end": v(54.26, 47.88) * mm});
            skLineSegment(sketch, "E95.0", {"start": v(60, 38.83) * mm, "end": v(60, -38.83) * mm});
            skArc(sketch, "E96.0", {"start": v(54.26, -47.88) * mm, "mid": v(58.44, -44.2) * mm, "end": v(60, -38.83) * mm});
            skArc(sketch, "E97.0", {"start": v(-54.26, -47.88) * mm, "mid": v(0, -60) * mm, "end": v(54.26, -47.88) * mm});
            skArc(sketch, "E98.0", {"start": v(-60, -38.83) * mm, "mid": v(-58.44, -44.2) * mm, "end": v(-54.26, -47.88) * mm});
            skLineSegment(sketch, "E99", {"start": v(-41.86, 90) * mm, "end": v(-23.86, 108) * mm});
            skLineSegment(sketch, "E100", {"start": v(-23.86, 108) * mm, "end": v(-23.86, 120) * mm});
            skArc(sketch, "E101", {"start": v(6.14, 120) * mm, "mid": v(-8.86, 135) * mm, "end": v(-23.86, 120) * mm});
            skLineSegment(sketch, "E102", {"start": v(6.14, 108) * mm, "end": v(24.14, 90) * mm});
            skCircle(sketch, "E103", {"center": v(-8.86, 120) * mm, "radius": 6 * mm});
            skLineSegment(sketch, "E104", {"start": v(6.14, 108) * mm, "end": v(6.14, 120) * mm});
            skLineSegment(sketch, "E105", {"start": v(-90, 0) * mm, "end": v(90, 0) * mm, "construction": true});
            skLineSegment(sketch, "E106.MirrorCS", {"start": v(-41.86, -90) * mm, "end": v(-23.86, -108) * mm});
            skLineSegment(sketch, "E107.MirrorCS", {"start": v(-23.86, -108) * mm, "end": v(-23.86, -120) * mm});
            skLineSegment(sketch, "E108.MirrorCS", {"start": v(6.14, -108) * mm, "end": v(6.14, -120) * mm});
            skArc(sketch, "E109.MirrorCS", {"start": v(6.14, -120) * mm, "mid": v(-8.86, -135) * mm, "end": v(-23.86, -120) * mm});
            skCircle(sketch, "E110.MirrorC", {"center": v(-8.86, -120) * mm, "radius": 6 * mm});
            skLineSegment(sketch, "E111.MirrorCS", {"start": v(6.14, -108) * mm, "end": v(24.14, -90) * mm});
            skLineSegment(sketch, "E112", {"start": v(-8.86, 120) * mm, "end": v(-8.86, 90) * mm, "construction": true});
            skLineSegment(sketch, "E113", {"start": v(-8.86, -120) * mm, "end": v(-8.86, -90) * mm, "construction": true});
            skSolve(sketch);
        }
        {
            var Q0;
            Q0 = qSketchRegion(id + "F16", true);
            var Q1;
            Q1=makeQuery(id+"F2.opExtrude","CAP_FACE",FACE,{"disambiguationData":[OSD([sQuery(id+"F0.wireOp",EDGE,"E12"),sQuery(id+"F0.wireOp",EDGE,"E13"),sQuery(id+"F0.wireOp",EDGE,"E14"),sQuery(id+"F0.wireOp",EDGE,"E15"),sQuery(id+"F0.wireOp",EDGE,"E17.filletArc"),sQuery(id+"F0.wireOp",EDGE,"E18.filletArc"),sQuery(id+"F0.wireOp",EDGE,"E19.filletArc"),sQuery(id+"F0.wireOp",EDGE,"E20.filletArc"),sQuery(id+"F0.wireOp",EDGE,"E25.0"),sQuery(id+"F0.wireOp",EDGE,"E25.1"),sQuery(id+"F0.wireOp",EDGE,"E25.2"),sQuery(id+"F0.wireOp",EDGE,"E25.3"),sQuery(id+"F0.wireOp",EDGE,"E25.4"),sQuery(id+"F0.wireOp",EDGE,"E25.5"),sQuery(id+"F0.wireOp",EDGE,"E25.6"),sQuery(id+"F0.wireOp",EDGE,"E25.7")])],"isStart":false});
            extrude(context, id + "F17", {"entities" : qUnion([Q0]), "endBound" : BoundingType.UP_TO_SURFACE, "endBoundEntityFace" : qUnion([Q1]), "depth" : 25 * mm});
        }
    });
